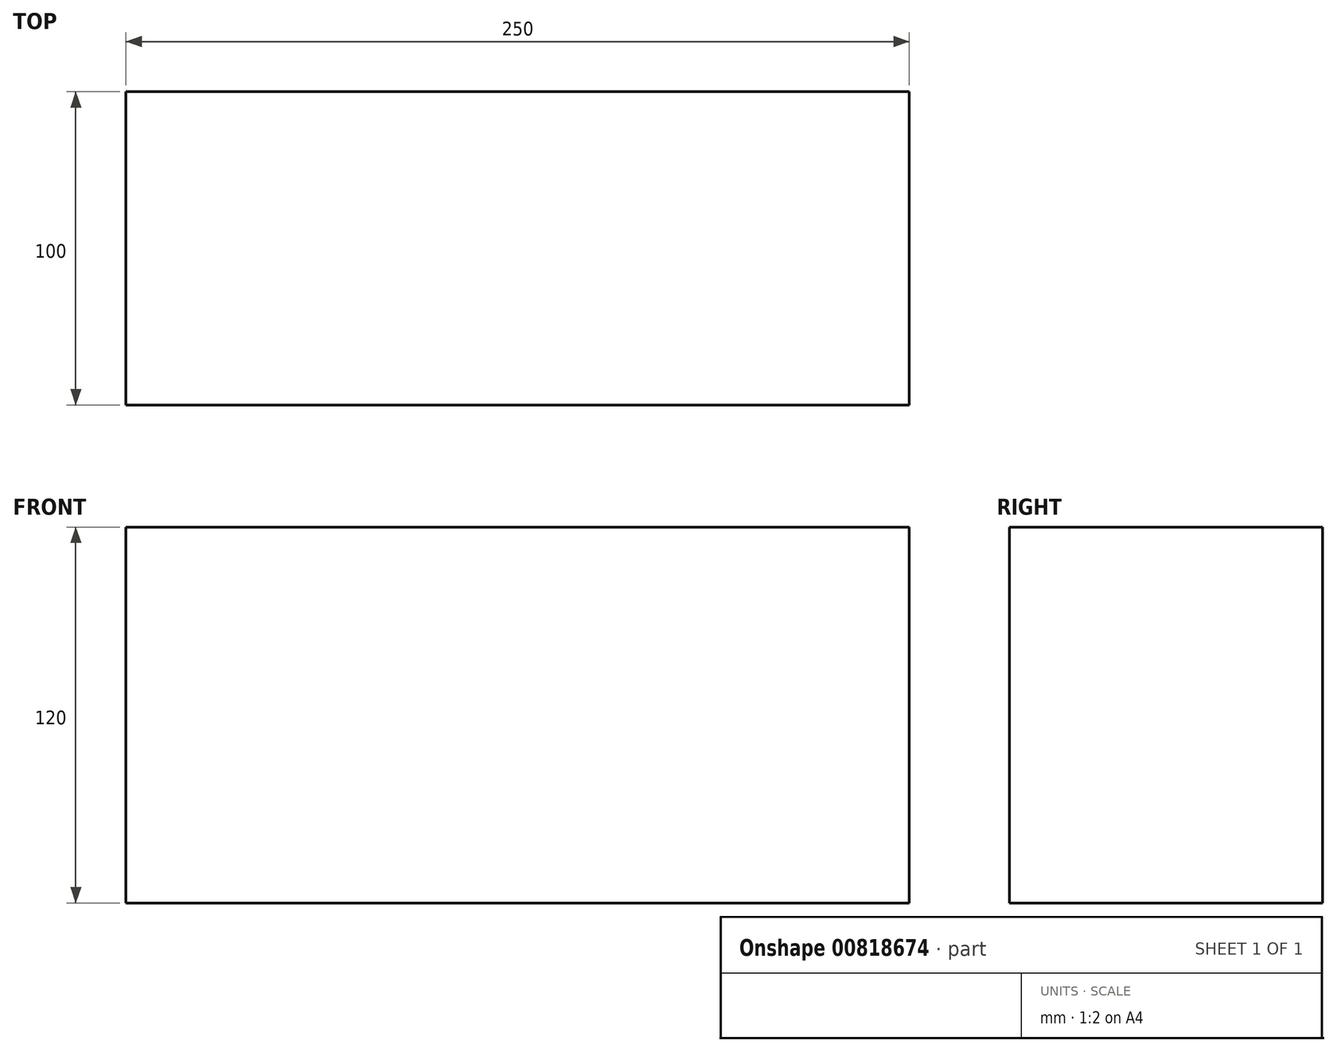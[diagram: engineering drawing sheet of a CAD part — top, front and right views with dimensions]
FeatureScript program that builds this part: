
annotation { "Feature Type Name" : "Feature", "Feature Type Description" : "" }
export const myFeature = defineFeature(function(context is Context, id is Id, definition is map)
    precondition{}
    {
        {
            var Q0;
            Q0=qCreatedBy(makeId("Front.planeOp"),FACE);
            var sketch = newSketch(context, id + "F0", { "sketchPlane" : qUnion([Q0])});
            skLineSegment(sketch, "E0", {"start": v(-157.16, 26.2) * mm, "end": v(-157.16, -93.8) * mm});
            skLineSegment(sketch, "E1", {"start": v(-157.16, -93.8) * mm, "end": v(92.84, -93.8) * mm});
            skLineSegment(sketch, "E2", {"start": v(92.84, -93.8) * mm, "end": v(92.84, 26.2) * mm});
            skLineSegment(sketch, "E3", {"start": v(92.84, 26.2) * mm, "end": v(-157.16, 26.2) * mm});
            skSolve(sketch);
        }
        {
            var Q0;
            Q0=makeQuery(id+"F0.imprint","IMPRINT",FACE,{"disambiguationData":[TD([[makeQuery(id+"F0.imprint","IMPRINT",EDGE,{"derivedFrom":sQuery(id+"F0.wireOp",EDGE,"E0")}),1.0]])]});
            extrude(context, id + "F1", {"entities" : qUnion([Q0]), "depth" : 100 * mm, "offsetDistance" : 25 * mm});
        }
    });
